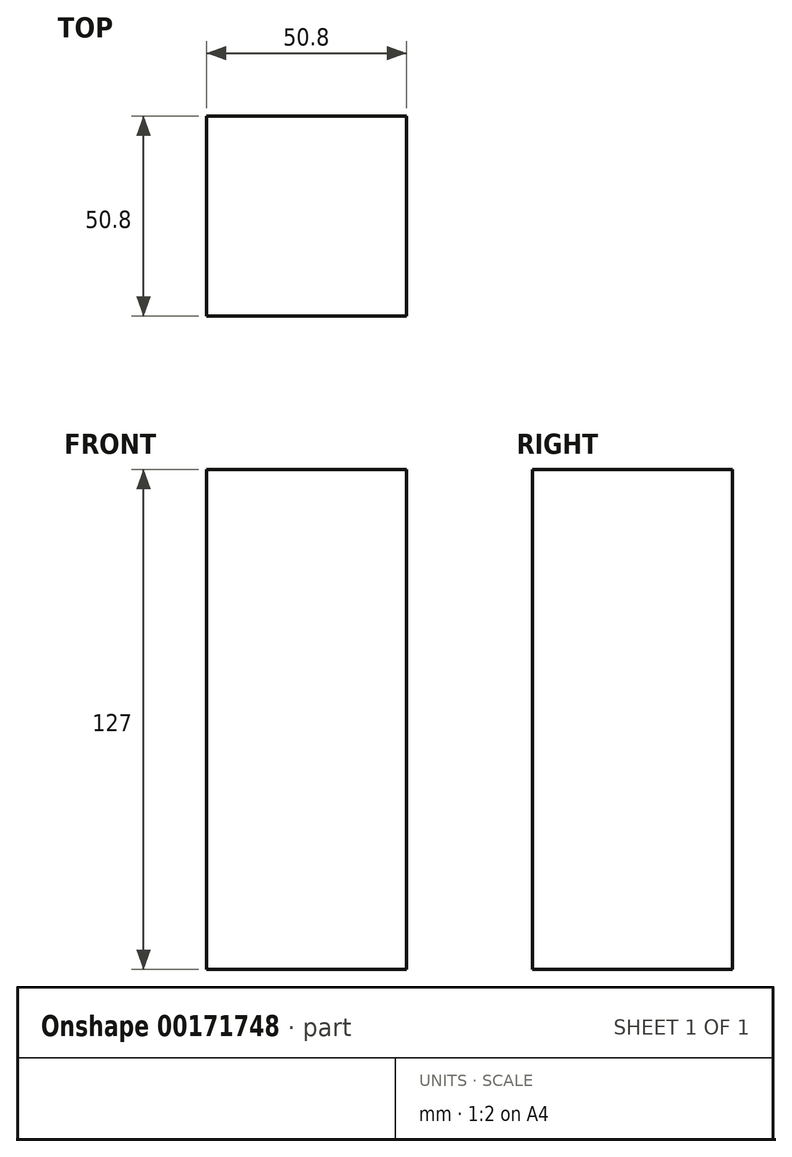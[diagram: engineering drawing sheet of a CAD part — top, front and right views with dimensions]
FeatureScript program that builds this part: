
annotation { "Feature Type Name" : "Feature", "Feature Type Description" : "" }
export const myFeature = defineFeature(function(context is Context, id is Id, definition is map)
    precondition{}
    {
        {
            var Q0;
            Q0=qCreatedBy(makeId("Top.planeOp"),FACE);
            var sketch = newSketch(context, id + "F0", { "sketchPlane" : qUnion([Q0])});
            skLineSegment(sketch, "E0.bottom", {"start": v(0, 0) * mm, "end": v(50.8, 0) * mm});
            skLineSegment(sketch, "E0.top", {"start": v(0, -50.8) * mm, "end": v(50.8, -50.8) * mm});
            skLineSegment(sketch, "E0.left", {"start": v(0, 0) * mm, "end": v(0, -50.8) * mm});
            skLineSegment(sketch, "E0.right", {"start": v(50.8, 0) * mm, "end": v(50.8, -50.8) * mm});
            skSolve(sketch);
        }
        {
            var Q0;
            Q0 = qSketchRegion(id + "F0", true);
            extrude(context, id + "F1", {"entities" : qUnion([Q0]), "depth" : 127 * mm});
        }
    });
